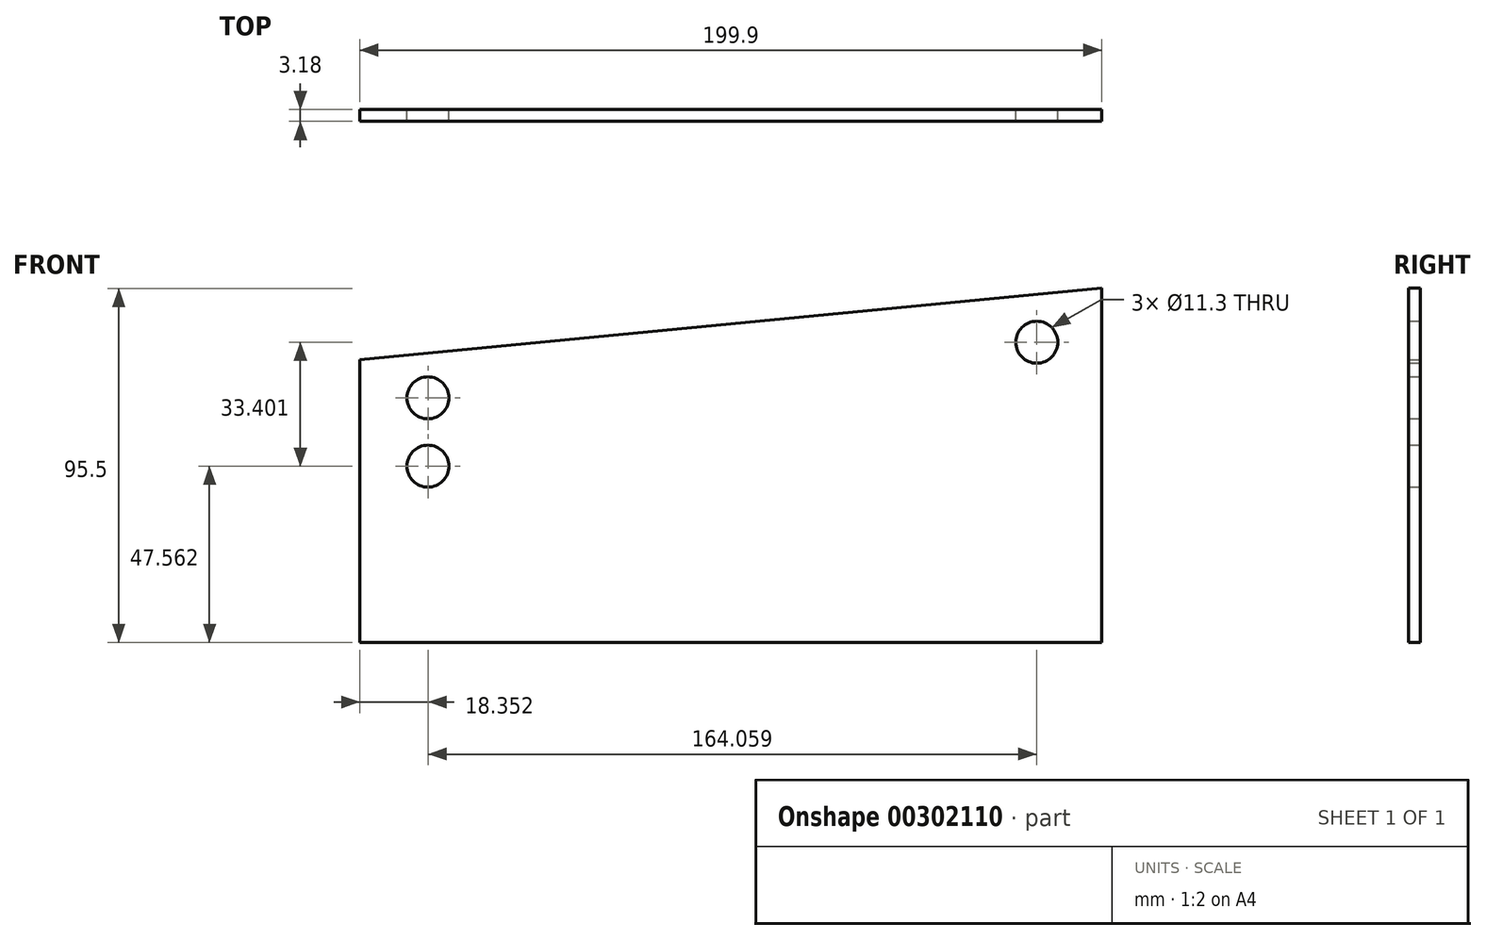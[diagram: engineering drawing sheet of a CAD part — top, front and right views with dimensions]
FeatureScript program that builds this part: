
annotation { "Feature Type Name" : "Feature", "Feature Type Description" : "" }
export const myFeature = defineFeature(function(context is Context, id is Id, definition is map)
    precondition{}
    {
        {
            var Q0;
            Q0=qCreatedBy(makeId("Front.planeOp"),FACE);
            var sketch = newSketch(context, id + "F0", { "sketchPlane" : qUnion([Q0])});
            skLineSegment(sketch, "E0.bottom", {"start": v(0, 0) * mm, "end": v(199.9, 0) * mm});
            skLineSegment(sketch, "E0.top", {"start": v(0, 76.2) * mm, "end": v(199.9, 76.2) * mm});
            skLineSegment(sketch, "E0.left", {"start": v(0, 0) * mm, "end": v(0, 76.2) * mm});
            skLineSegment(sketch, "E0.right", {"start": v(199.9, 0) * mm, "end": v(199.9, 76.2) * mm});
            skLineSegment(sketch, "E1", {"start": v(199.9, 76.2) * mm, "end": v(199.9, 95.5) * mm});
            skLineSegment(sketch, "E2", {"start": v(0, 76.2) * mm, "end": v(199.9, 95.5) * mm});
            skCircle(sketch, "E3", {"center": v(182.41, 80.96) * mm, "radius": 5.65 * mm});
            skCircle(sketch, "E4", {"center": v(18.35, 65.98) * mm, "radius": 5.65 * mm});
            skCircle(sketch, "E5", {"center": v(18.35, 47.56) * mm, "radius": 5.65 * mm});
            skSolve(sketch);
        }
        {
            var Q0;
            Q0=makeQuery(id+"F0.imprint","IMPRINT",FACE,{"disambiguationData":[TD([[makeQuery(id+"F0.imprint","IMPRINT",EDGE,{"derivedFrom":sQuery(id+"F0.wireOp",EDGE,"E0.bottom")}),1.0]])]});
            var Q1;
            {var subQ1=sQuery(id+"F0.wireOp",EDGE,"E1");Q1=makeQuery(id+"F0.imprint","IMPRINT",FACE,{"disambiguationData":[TD([[makeQuery(id+"F0.imprint","IMPRINT",EDGE,{"derivedFrom":subQ1}),1.0]])]});}
            extrude(context, id + "F1", {"entities" : qUnion([Q0, Q1]), "depth" : 3.17 * mm});
        }
    });
